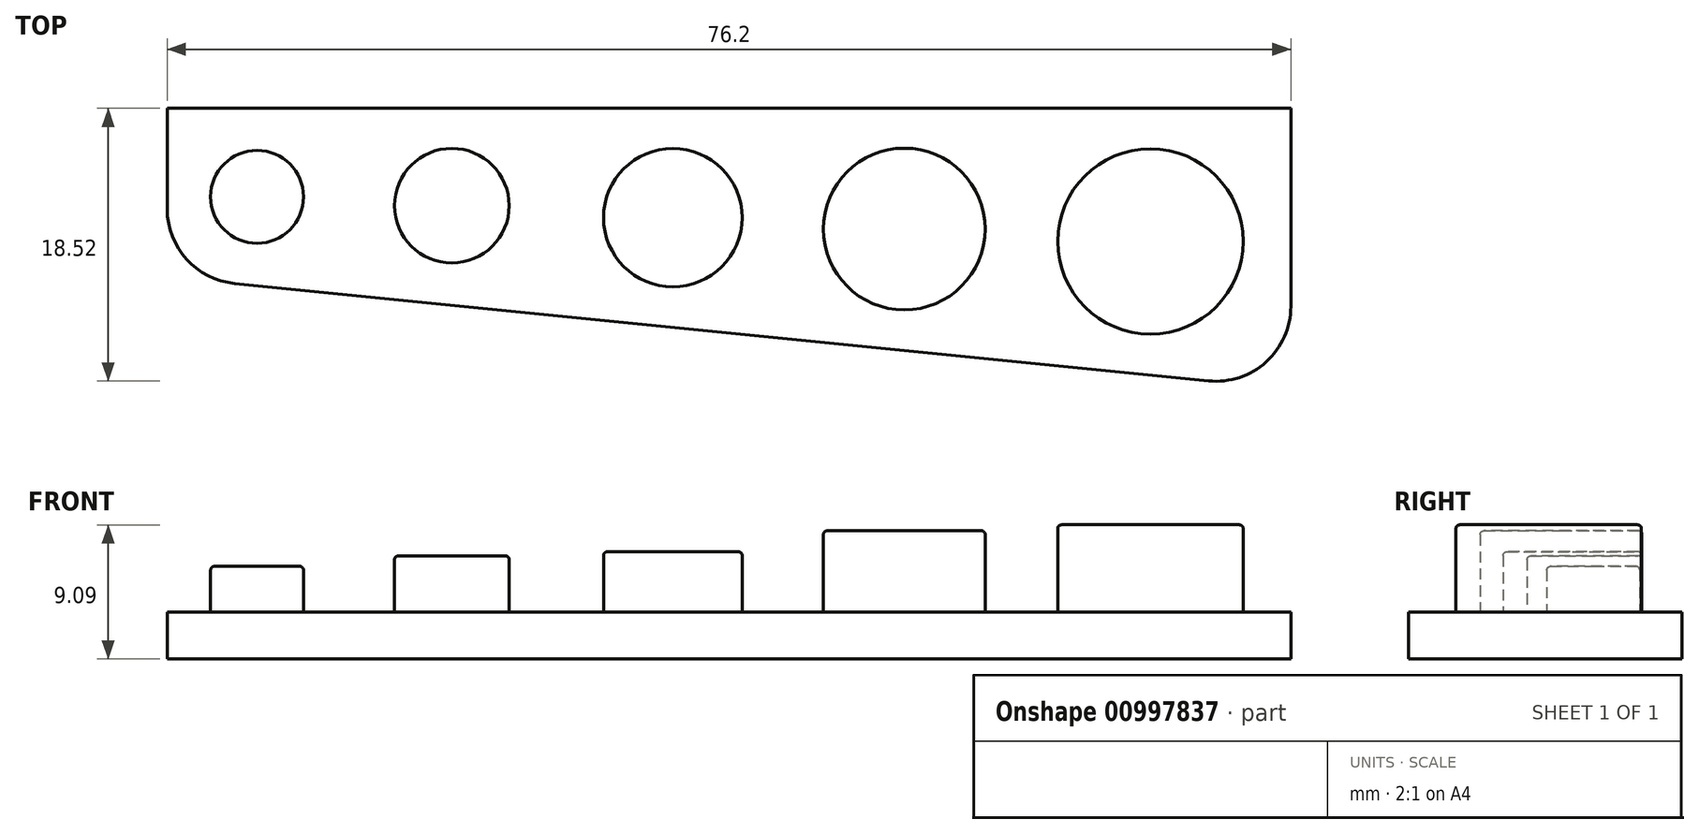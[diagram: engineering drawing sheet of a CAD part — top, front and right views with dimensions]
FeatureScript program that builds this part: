
annotation { "Feature Type Name" : "Feature", "Feature Type Description" : "" }
export const myFeature = defineFeature(function(context is Context, id is Id, definition is map)
    precondition{}
    {
        {
            var Q0;
            Q0=qCreatedBy(makeId("Top.planeOp"),FACE);
            var sketch = newSketch(context, id + "F0", { "sketchPlane" : qUnion([Q0])});
            skLineSegment(sketch, "E0", {"start": v(39.67, 7.53) * mm, "end": v(-36.53, 7.53) * mm});
            skLineSegment(sketch, "E1", {"start": v(39.67, 7.53) * mm, "end": v(39.67, -11.52) * mm});
            skLineSegment(sketch, "E2", {"start": v(-36.53, 7.53) * mm, "end": v(-36.53, -3.9) * mm});
            skLineSegment(sketch, "E3", {"start": v(-36.53, -3.9) * mm, "end": v(39.67, -11.52) * mm});
            skCircle(sketch, "E4", {"center": v(13.46, -0.67) * mm, "radius": 5.49 * mm});
            skCircle(sketch, "E5", {"center": v(-2.24, 0.1) * mm, "radius": 4.7 * mm});
            skCircle(sketch, "E6", {"center": v(-17.22, 0.92) * mm, "radius": 3.89 * mm});
            skCircle(sketch, "E7", {"center": v(30.15, -1.5) * mm, "radius": 6.29 * mm});
            skCircle(sketch, "E8", {"center": v(-30.43, 1.52) * mm, "radius": 3.15 * mm});
            skSolve(sketch);
        }
        {
            var Q0;
            Q0=makeQuery(id+"F0.imprint","IMPRINT",FACE,{"disambiguationData":[TD([[makeQuery(id+"F0.imprint","IMPRINT",EDGE,{"derivedFrom":sQuery(id+"F0.wireOp",EDGE,"E0")}),1.0]])]});
            var sketch = newSketch(context, id + "F1", { "sketchPlane" : qUnion([Q0])});
            skSolve(sketch);
        }
        {
            var Q0;
            Q0=makeQuery(id+"F1.imprint","IMPRINT",FACE,{"disambiguationData":[TD([[makeQuery(id+"F1.imprint","IMPRINT",EDGE,{"derivedFrom":makeQuery(id+"F0.imprint","IMPRINT",EDGE,{"derivedFrom":sQuery(id+"F0.wireOp",EDGE,"E0")})}),1.0]])]});
            var sketch = newSketch(context, id + "F2", { "sketchPlane" : qUnion([Q0])});
            skSolve(sketch);
        }
        {
            var Q0;
            Q0=makeQuery(id+"F2.imprint","IMPRINT",FACE,{"disambiguationData":[TD([[makeQuery(id+"F2.imprint","IMPRINT",EDGE,{"derivedFrom":makeQuery(id+"F1.imprint","IMPRINT",EDGE,{"derivedFrom":makeQuery(id+"F0.imprint","IMPRINT",EDGE,{"derivedFrom":sQuery(id+"F0.wireOp",EDGE,"E0")})})}),1.0]])]});
            var Q1;
            Q1=makeQuery(id+"F2.imprint","IMPRINT",FACE,{"disambiguationData":[TD([[makeQuery(id+"F2.imprint","IMPRINT",EDGE,{"derivedFrom":makeQuery(id+"F1.imprint","IMPRINT",EDGE,{"derivedFrom":makeQuery(id+"F0.imprint","IMPRINT",EDGE,{"derivedFrom":sQuery(id+"F0.wireOp",EDGE,"E7")})})}),1.0]])]});
            var Q2;
            Q2=makeQuery(id+"F2.imprint","IMPRINT",FACE,{"disambiguationData":[TD([[makeQuery(id+"F2.imprint","IMPRINT",EDGE,{"derivedFrom":makeQuery(id+"F1.imprint","IMPRINT",EDGE,{"derivedFrom":makeQuery(id+"F0.imprint","IMPRINT",EDGE,{"derivedFrom":sQuery(id+"F0.wireOp",EDGE,"E4")})})}),1.0]])]});
            var Q3;
            Q3=makeQuery(id+"F2.imprint","IMPRINT",FACE,{"disambiguationData":[TD([[makeQuery(id+"F2.imprint","IMPRINT",EDGE,{"derivedFrom":makeQuery(id+"F1.imprint","IMPRINT",EDGE,{"derivedFrom":makeQuery(id+"F0.imprint","IMPRINT",EDGE,{"derivedFrom":sQuery(id+"F0.wireOp",EDGE,"E5")})})}),1.0]])]});
            var Q4;
            Q4=makeQuery(id+"F2.imprint","IMPRINT",FACE,{"disambiguationData":[TD([[makeQuery(id+"F2.imprint","IMPRINT",EDGE,{"derivedFrom":makeQuery(id+"F1.imprint","IMPRINT",EDGE,{"derivedFrom":makeQuery(id+"F0.imprint","IMPRINT",EDGE,{"derivedFrom":sQuery(id+"F0.wireOp",EDGE,"E6")})})}),1.0]])]});
            var Q5;
            Q5=makeQuery(id+"F2.imprint","IMPRINT",FACE,{"disambiguationData":[TD([[makeQuery(id+"F2.imprint","IMPRINT",EDGE,{"derivedFrom":makeQuery(id+"F1.imprint","IMPRINT",EDGE,{"derivedFrom":makeQuery(id+"F0.imprint","IMPRINT",EDGE,{"derivedFrom":sQuery(id+"F0.wireOp",EDGE,"E8")})})}),1.0]])]});
            extrude(context, id + "F3", {"entities" : qUnion([Q0, Q1, Q2, Q3, Q4, Q5]), "depth" : 3.17 * mm, "offsetDistance" : 25.4 * mm});
        }
        {
            var Q0;
            Q0=makeQuery(id+"F1.imprint","IMPRINT",FACE,{"disambiguationData":[TD([[makeQuery(id+"F1.imprint","IMPRINT",EDGE,{"derivedFrom":makeQuery(id+"F0.imprint","IMPRINT",EDGE,{"derivedFrom":sQuery(id+"F0.wireOp",EDGE,"E7")})}),1.0]])]});
            extrude(context, id + "F4", {"entities" : qUnion([Q0]), "operationType" : NewBodyOperationType.ADD, "depth" : 9.1 * mm, "offsetDistance" : 25.4 * mm});
        }
        {
            var Q0;
            Q0=makeQuery(id+"F0.imprint","IMPRINT",FACE,{"disambiguationData":[TD([[makeQuery(id+"F0.imprint","IMPRINT",EDGE,{"derivedFrom":sQuery(id+"F0.wireOp",EDGE,"E4")}),1.0]])]});
            extrude(context, id + "F5", {"entities" : qUnion([Q0]), "operationType" : NewBodyOperationType.ADD, "depth" : 8.7 * mm, "offsetDistance" : 25.4 * mm});
        }
        {
            var Q0;
            Q0=makeQuery(id+"F2.imprint","IMPRINT",FACE,{"disambiguationData":[TD([[makeQuery(id+"F2.imprint","IMPRINT",EDGE,{"derivedFrom":makeQuery(id+"F1.imprint","IMPRINT",EDGE,{"derivedFrom":makeQuery(id+"F0.imprint","IMPRINT",EDGE,{"derivedFrom":sQuery(id+"F0.wireOp",EDGE,"E5")})})}),1.0]])]});
            extrude(context, id + "F6", {"entities" : qUnion([Q0]), "operationType" : NewBodyOperationType.ADD, "depth" : 7.26 * mm, "offsetDistance" : 25.4 * mm});
        }
        {
            var Q0;
            Q0=makeQuery(id+"F2.imprint","IMPRINT",FACE,{"disambiguationData":[TD([[makeQuery(id+"F2.imprint","IMPRINT",EDGE,{"derivedFrom":makeQuery(id+"F1.imprint","IMPRINT",EDGE,{"derivedFrom":makeQuery(id+"F0.imprint","IMPRINT",EDGE,{"derivedFrom":sQuery(id+"F0.wireOp",EDGE,"E6")})})}),1.0]])]});
            extrude(context, id + "F7", {"entities" : qUnion([Q0]), "operationType" : NewBodyOperationType.ADD, "depth" : 7 * mm, "offsetDistance" : 25.4 * mm});
        }
        {
            var Q0;
            Q0=makeQuery(id+"F2.imprint","IMPRINT",FACE,{"disambiguationData":[TD([[makeQuery(id+"F2.imprint","IMPRINT",EDGE,{"derivedFrom":makeQuery(id+"F1.imprint","IMPRINT",EDGE,{"derivedFrom":makeQuery(id+"F0.imprint","IMPRINT",EDGE,{"derivedFrom":sQuery(id+"F0.wireOp",EDGE,"E8")})})}),1.0]])]});
            extrude(context, id + "F8", {"entities" : qUnion([Q0]), "operationType" : NewBodyOperationType.ADD, "depth" : 6.27 * mm, "offsetDistance" : 25.4 * mm});
        }
        {
            var Q0;
            Q0=makeQuery(id+"F3.opExtrude","SWEPT_EDGE",EDGE,{"disambiguationData":[OSD([sQuery(id+"F0.wireOp",EDGE,"E1"),sQuery(id+"F0.wireOp",EDGE,"E3")])]});
            var Q1;
            Q1=makeQuery(id+"F3.opExtrude","SWEPT_EDGE",EDGE,{"disambiguationData":[OSD([sQuery(id+"F0.wireOp",EDGE,"E2"),sQuery(id+"F0.wireOp",EDGE,"E3")])]});
            fillet(context, id + "F9", {"entities" : qUnion([Q0, Q1]), "radius" : 5.08 * mm, "tangentPropagation" : true, "allowEdgeOverflow" : false});
        }
        {
            var Q0;
            Q0=makeQuery(id+"F4.opExtrude","CAP_EDGE",EDGE,{"disambiguationData":[OSD([sQuery(id+"F0.wireOp",EDGE,"E7")])],"isStart":false});
            var Q1;
            Q1=makeQuery(id+"F5.opExtrude","CAP_EDGE",EDGE,{"disambiguationData":[OSD([sQuery(id+"F0.wireOp",EDGE,"E4")])],"isStart":false});
            var Q2;
            Q2=makeQuery(id+"F6.opExtrude","CAP_EDGE",EDGE,{"disambiguationData":[OSD([sQuery(id+"F0.wireOp",EDGE,"E5")])],"isStart":false});
            var Q3;
            Q3=makeQuery(id+"F7.opExtrude","CAP_EDGE",EDGE,{"disambiguationData":[OSD([sQuery(id+"F0.wireOp",EDGE,"E6")])],"isStart":false});
            var Q4;
            Q4=makeQuery(id+"F8.opExtrude","CAP_EDGE",EDGE,{"disambiguationData":[OSD([sQuery(id+"F0.wireOp",EDGE,"E8")])],"isStart":false});
            fillet(context, id + "F10", {"entities" : qUnion([Q0, Q1, Q2, Q3, Q4]), "radius" : 0.25 * mm, "tangentPropagation" : true, "allowEdgeOverflow" : false});
        }
    });
